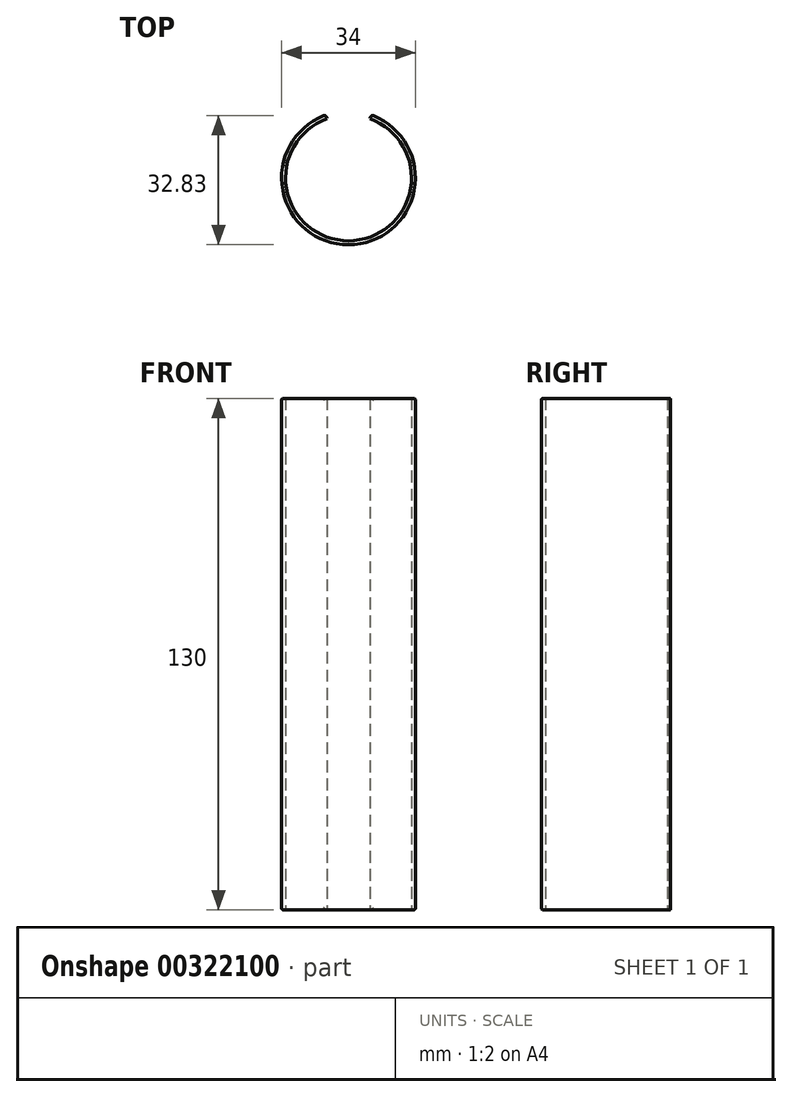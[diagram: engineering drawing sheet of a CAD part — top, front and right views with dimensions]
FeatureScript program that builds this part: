
annotation { "Feature Type Name" : "Feature", "Feature Type Description" : "" }
export const myFeature = defineFeature(function(context is Context, id is Id, definition is map)
    precondition{}
    {
        {
            var Q0;
            Q0=qCreatedBy(makeId("Top.planeOp"),FACE);
            var sketch = newSketch(context, id + "F0", { "sketchPlane" : qUnion([Q0])});
            skArc(sketch, "E0", {"start": v(-5.47, 15.04) * mm, "mid": v(0, -16) * mm, "end": v(5.47, 15.04) * mm});
            skArc(sketch, "E1", {"start": v(-5.81, 15.97) * mm, "mid": v(0, -17) * mm, "end": v(5.81, 15.97) * mm});
            skLineSegment(sketch, "E2", {"start": v(-5.47, 15.04) * mm, "end": v(-5.81, 15.97) * mm});
            skLineSegment(sketch, "E3", {"start": v(5.47, 15.04) * mm, "end": v(5.81, 15.97) * mm});
            skSolve(sketch);
        }
        {
            var Q0;
            Q0 = qSketchRegion(id + "F0", true);
            extrude(context, id + "F1", {"entities" : qUnion([Q0]), "depth" : 130 * mm});
        }
        {
            var Q0;
            Q0=makeQuery(id+"F1.opExtrude","SWEPT_FACE",FACE,{"disambiguationData":[OSD([sQuery(id+"F0.wireOp",EDGE,"E1")])]});
            fillet(context, id + "F2", {"entities" : qUnion([Q0]), "radius" : 0.5 * mm, "tangentPropagation" : true, "allowEdgeOverflow" : false});
        }
    });
